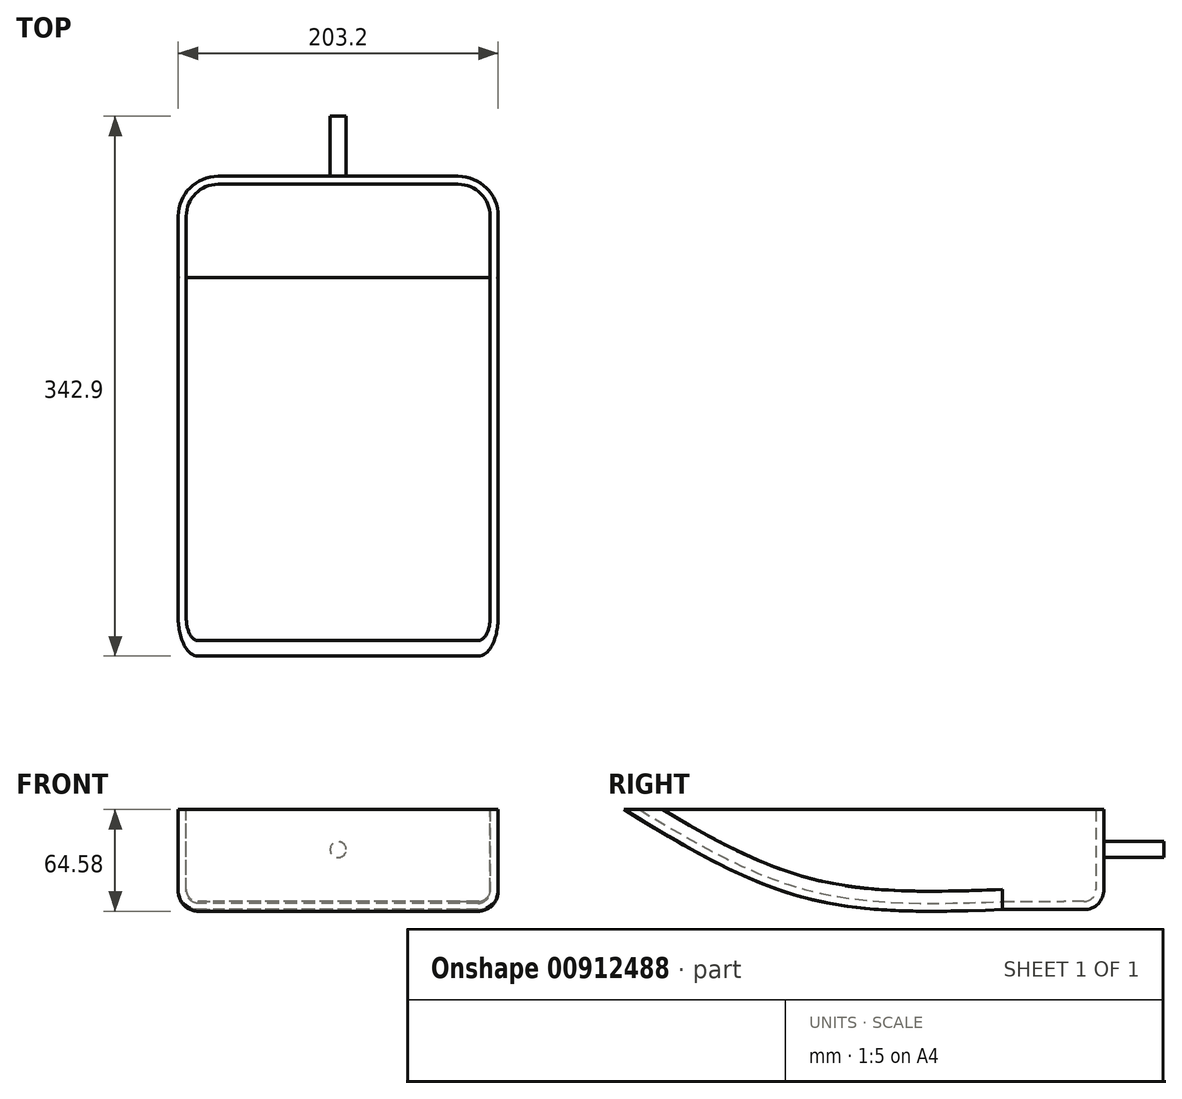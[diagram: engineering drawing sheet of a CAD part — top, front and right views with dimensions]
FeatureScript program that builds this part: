
annotation { "Feature Type Name" : "Feature", "Feature Type Description" : "" }
export const myFeature = defineFeature(function(context is Context, id is Id, definition is map)
    precondition{}
    {
        {
            var Q0;
            Q0=qCreatedBy(makeId("Right.planeOp"),FACE);
            var sketch = newSketch(context, id + "F0", { "sketchPlane" : qUnion([Q0])});
            skLineSegment(sketch, "E0", {"start": v(13.56, 0) * mm, "end": v(13.56, 49.94) * mm});
            skLineSegment(sketch, "E1", {"start": v(13.56, 49.94) * mm, "end": v(-291.24, 49.94) * mm});
            skLineSegment(sketch, "E2", {"start": v(0, -13.56) * mm, "end": v(-50.8, -13.56) * mm});
            skFitSpline(sketch, "E3", {"points": [v(-291.24, 49.94) * mm, v(-176.21, -6.13) * mm, v(-50.8, -13.56) * mm], "startDerivative": vector(223.22, -135.9) * mm, "endDerivative": vector(257.7, 9.13) * mm});
            skLineSegment(sketch, "E4", {"start": v(13.56, 0) * mm, "end": v(13.56, -13.56) * mm});
            skLineSegment(sketch, "E5", {"start": v(13.56, -13.56) * mm, "end": v(0, -13.56) * mm});
            skSolve(sketch);
        }
        {
            var Q0;
            Q0=makeQuery(id+"F0.imprint","IMPRINT",FACE,{"disambiguationData":[TD([[makeQuery(id+"F0.imprint","IMPRINT",EDGE,{"derivedFrom":sQuery(id+"F0.wireOp",EDGE,"E0")}),1.0]])]});
            extrude(context, id + "F1", {"entities" : qUnion([Q0]), "depth" : 203.2 * mm, "offsetDistance" : 25.4 * mm});
        }
        {
            var Q0;
            Q0=makeQuery(id+"F1.opExtrude","SWEPT_FACE",FACE,{"disambiguationData":[OSD([sQuery(id+"F0.wireOp",EDGE,"E0"),sQuery(id+"F0.wireOp",EDGE,"E4")])]});
            var sketch = newSketch(context, id + "F2", { "sketchPlane" : qUnion([Q0])});
            skCircle(sketch, "E6", {"center": v(-101.6, 24.54) * mm, "radius": 5.08 * mm});
            skSolve(sketch);
        }
        {
            var Q0;
            Q0=makeQuery(id+"F2.imprint","IMPRINT",FACE,{"disambiguationData":[TD([[makeQuery(id+"F2.imprint","IMPRINT",EDGE,{"derivedFrom":sQuery(id+"F2.wireOp",EDGE,"E6")}),1.0]])]});
            extrude(context, id + "F3", {"entities" : qUnion([Q0]), "operationType" : NewBodyOperationType.ADD, "depth" : 38.1 * mm, "offsetDistance" : 25.4 * mm});
        }
        {
            var Q0;
            Q0=makeQuery(id+"F1.opExtrude","CAP_EDGE",EDGE,{"disambiguationData":[OSD([sQuery(id+"F0.wireOp",EDGE,"E0"),sQuery(id+"F0.wireOp",EDGE,"E4")])],"isStart":false});
            var Q1;
            Q1=makeQuery(id+"F1.opExtrude","CAP_EDGE",EDGE,{"disambiguationData":[OSD([sQuery(id+"F0.wireOp",EDGE,"E0"),sQuery(id+"F0.wireOp",EDGE,"E4")])],"isStart":true});
            fillet(context, id + "F4", {"entities" : qUnion([Q0, Q1]), "radius" : 25.4 * mm, "tangentPropagation" : true, "allowEdgeOverflow" : false});
        }
        {
            var Q0;
            Q0=makeQuery(id+"F1.opExtrude","SWEPT_EDGE",EDGE,{"disambiguationData":[OSD([sQuery(id+"F0.wireOp",EDGE,"E4"),sQuery(id+"F0.wireOp",EDGE,"E5")])]});
            fillet(context, id + "F5", {"entities" : qUnion([Q0]), "radius" : 12.7 * mm, "tangentPropagation" : true, "allowEdgeOverflow" : false});
        }
        {
            var Q0;
            Q0=makeQuery(id+"F1.opExtrude","SWEPT_FACE",FACE,{"disambiguationData":[OSD([sQuery(id+"F0.wireOp",EDGE,"E1")])]});
            shell(context, id + "F6", {"entities" : qUnion([Q0]), "thickness" : 5.08 * mm});
        }
    });
